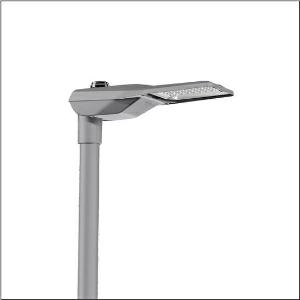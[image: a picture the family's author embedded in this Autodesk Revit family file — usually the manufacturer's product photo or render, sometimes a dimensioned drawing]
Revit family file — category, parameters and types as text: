
# Revit family: streetlight_sl_21_mini___st0_5a_5xe6b47n08jb_72a7
name_source: partatom
category: Lighting Fixtures
units: mm (PartAtom-declared; Revit-internal decimal feet)

## family parameters
Cut with Voids When Loaded = No
Host = Face
Light Source = No
Part Type = Normal
Room Calculation Point = No
Round Connector Dimension = Use Diameter
Shared = No

## types (1)
- --- (1 x LED, 13390 lm, 87.3 W, 4000K)
    Apparent Load = 87 VA
    CIE Flux Codes = 43 76 97 100 100
    Color Rendering = 70
    Color Temperature = 4000K
    Default Elevation = 1800 mm
    Description = Streetlight SL 21 mini, mast luminaire, primary light control with lens, of PMMA, primary optical cover: cover, of toughened safety glass, transparent, light distribution: ST0.5a, light emission: direct distribution, primary light characteristic: asymmetric, installation type: side-entry, LED, 3G 2.5mm², High Power LED, rated luminous flux: 13.390lm, luminous efficacy: 153lm/W, light colour: 740, colour temperature: 4000K, control gear: NEMA (7pin), control: overheat protection, pre-setting: linear dimming characteristic, constant luminous flux control, time-dependent luminous flux control, flexible luminous flux parameterisation, mains connection: 230..240V, AC, 50/60Hz, connection cable pre-assembled, cable length: 10,5m, wiring characteristics: H05VV-F, start of lifetime: 87W, end of service life: 90W, reduction: 40W, luminaire housing, of diecast aluminium (EN AC-44300), powder-coated, Siteco® metallic grey (DB 702S), corrosivity category C5 high according to DIN EN ISO 12944, multi-level sealing system, sealing non-destructively replaceable, inclination adjustable: 0°, 5°, 10°, 15°, length: 628mm, width: 235mm, height: 110mm, spigot size: 42mm (side-entry), mounting height: 4..8m, protection rating (complete): IP66, insulation class (complete): insulation class I (protective earthing), certification: CE, ENEC, ENEC+, VDE, impact resistance: IK10, permissible operating ambient temperature for outdoor applications: -40..+50°C, standard-compliant lighting for roads and squares, packaging unit: 1 piece

Light Distribution: ST0.5a
    Height = 110 mm
    Lamp = 1 x LED
    Lamp Light Flux = 13390 lm
    Lamp Power = 87.3 W
    Lamp count = 1
    Length = 625 mm
    Luminous efficacy = 153 lm/W
    Manufacturer = Siteco
    ModVariant = No
    Model = 5XE6B47N08JB
    Number of Poles = 1
    OnlyDefault = Yes
    Power Factor = 1
    Product Name = Streetlight SL 21 mini | ST0.5a
    Product group = mast luminaire | pylon top
    ProductGroupID = 6100
    Protection Class = Protection class I
    Protection Degree = IP 66
    RLX_Detail_Level = 1
    RLX_Emergency_Light_Flux = 0 lm
    RLX_Emergency_Type = 0
    RLX_Emergency_Type_DB = No
    RlxData = <blob elided: 37245 chars, md5=5bbaf465>
    Socket = socket
    Standby Power = 0 W
    System Light Flux = 13390 lm
    System Power = 87 W
    Type Comments = factory setting: luminous flux: 100 % | dim-lin: 254 | 915 mA
    Type Image = l_1294379.jpg
    URL = http://relux.com
    VarID = @adj_140007
    Voltage = 0 V
    Weight = 0.00 kg
    Width = 234 mm

## geometry (parser evidence)
native form markers: Blend x4, Sweep x11
no freeform markers — native parametric forms only
